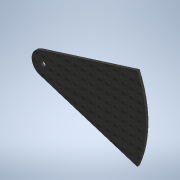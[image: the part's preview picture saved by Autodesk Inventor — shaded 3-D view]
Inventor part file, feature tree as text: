
AUTODESK INVENTOR PART (.ipt)
format: ipt  version: 2020 (Build 240168000, 168)  size: 114,176 bytes
history: native  units: in
note: dims shown in document units (in); Inventor stores cm internally (conversion verified against a paired STEP export)
features: extrude x1, sketch x1
ambient origin geometry x8: Origin, YZ Plane, XZ Plane, XY Plane, X Axis, Y Axis, Z Axis, Center Point
bodies: Solid1 (feature_tree)
feature tree (2):
  extrude  "Extrusion1"  Depth=1.9685in
  sketch  "Sketch3"  dims[d8=3.937in d9=19.685in d10=177.1654in d11=0.2405in d12=1.9685in d13=0.0in]
